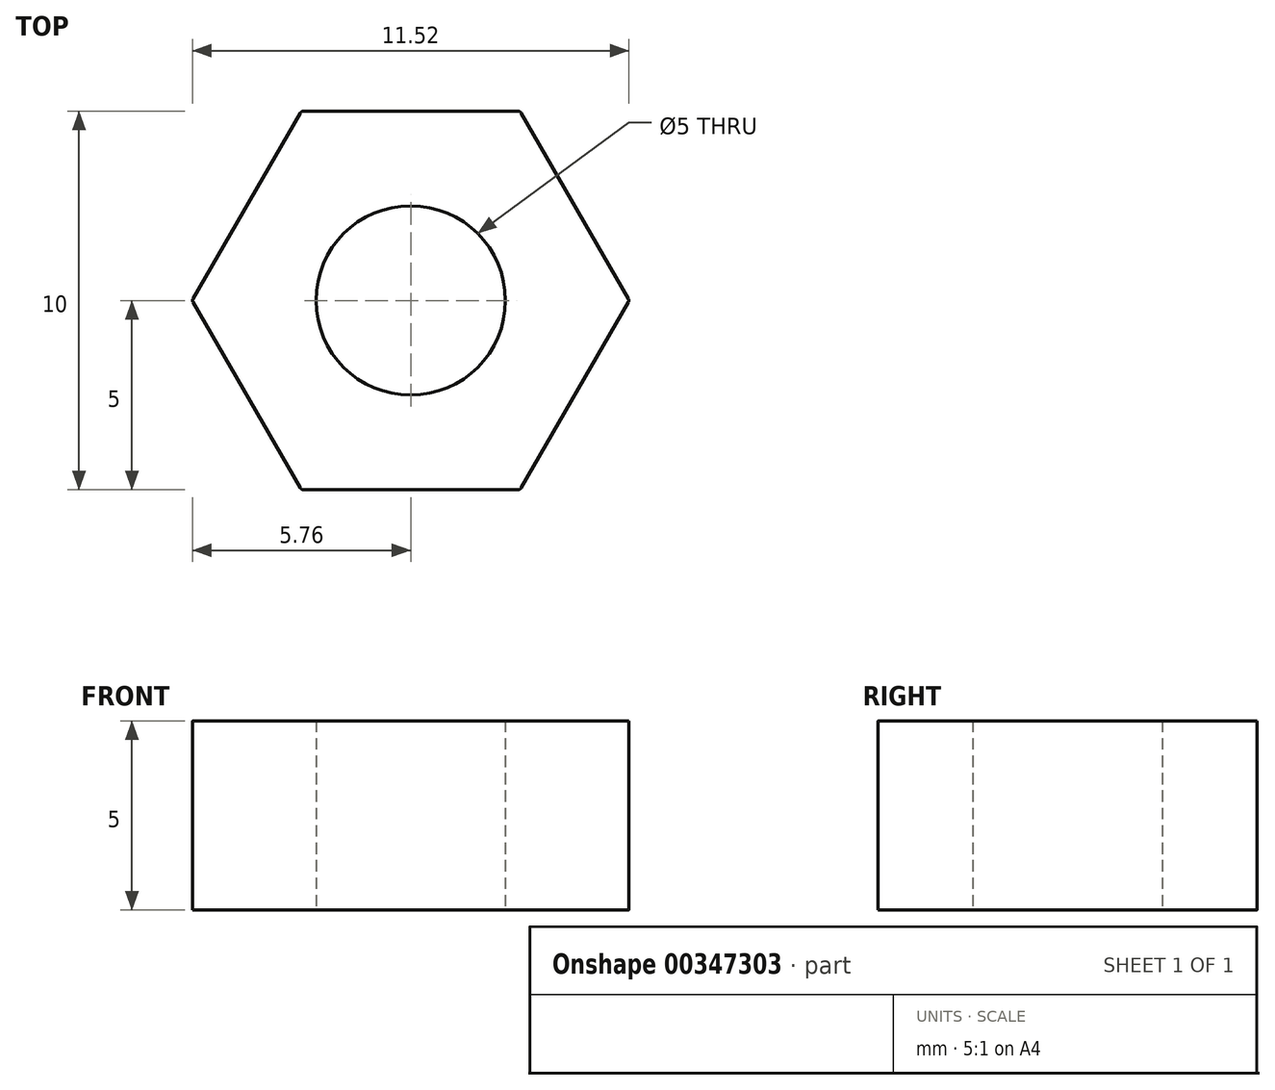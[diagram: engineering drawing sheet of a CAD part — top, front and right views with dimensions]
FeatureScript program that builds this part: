
annotation { "Feature Type Name" : "Feature", "Feature Type Description" : "" }
export const myFeature = defineFeature(function(context is Context, id is Id, definition is map)
    precondition{}
    {
        {
            var Q0;
            Q0=qCreatedBy(makeId("Top.planeOp"),FACE);
            var sketch = newSketch(context, id + "F0", { "sketchPlane" : qUnion([Q0])});
            skCircle(sketch, "E0.cCircle", {"center": v(0, 0) * mm, "radius": 5 * mm, "construction": true});
            skLineSegment(sketch, "E0.0", {"start": v(5.77, 0) * mm, "end": v(2.89, -5) * mm});
            skLineSegment(sketch, "E0.1", {"start": v(2.89, -5) * mm, "end": v(-2.89, -5) * mm});
            skLineSegment(sketch, "E0.2", {"start": v(-2.89, -5) * mm, "end": v(-5.77, 0) * mm});
            skLineSegment(sketch, "E0.3", {"start": v(-5.77, 0) * mm, "end": v(-2.89, 5) * mm});
            skLineSegment(sketch, "E0.4", {"start": v(-2.89, 5) * mm, "end": v(2.89, 5) * mm});
            skLineSegment(sketch, "E0.5", {"start": v(2.89, 5) * mm, "end": v(5.77, 0) * mm});
            skPoint(sketch, "E0.0.midPoint", {"position": v(4.33, -2.5) * mm});
            skCircle(sketch, "E1", {"center": v(0, 0) * mm, "radius": 2.5 * mm});
            skSolve(sketch);
        }
        {
            var Q0;
            Q0 = qSketchRegion(id + "F0", true);
            extrude(context, id + "F1", {"entities" : qUnion([Q0]), "depth" : 5 * mm});
        }
        {
            var Q0;
            Q0=makeQuery(id+"F1.opExtrude","SWEPT_EDGE",EDGE,{"disambiguationData":[OSD([sQuery(id+"F0.wireOp",EDGE,"E0.0"),sQuery(id+"F0.wireOp",EDGE,"E0.5")])]});
            var Q1;
            Q1=makeQuery(id+"F1.opExtrude","SWEPT_EDGE",EDGE,{"disambiguationData":[OSD([sQuery(id+"F0.wireOp",EDGE,"E0.4"),sQuery(id+"F0.wireOp",EDGE,"E0.5")])]});
            var Q2;
            Q2=makeQuery(id+"F1.opExtrude","SWEPT_EDGE",EDGE,{"disambiguationData":[OSD([sQuery(id+"F0.wireOp",EDGE,"E0.3"),sQuery(id+"F0.wireOp",EDGE,"E0.4")])]});
            var Q3;
            Q3=makeQuery(id+"F1.opExtrude","SWEPT_EDGE",EDGE,{"disambiguationData":[OSD([sQuery(id+"F0.wireOp",EDGE,"E0.0"),sQuery(id+"F0.wireOp",EDGE,"E0.1")])]});
            var Q4;
            Q4=makeQuery(id+"F1.opExtrude","SWEPT_EDGE",EDGE,{"disambiguationData":[OSD([sQuery(id+"F0.wireOp",EDGE,"E0.2"),sQuery(id+"F0.wireOp",EDGE,"E0.3")])]});
            var Q5;
            Q5=makeQuery(id+"F1.opExtrude","SWEPT_EDGE",EDGE,{"disambiguationData":[OSD([sQuery(id+"F0.wireOp",EDGE,"E0.1"),sQuery(id+"F0.wireOp",EDGE,"E0.2")])]});
            fillet(context, id + "F2", {"entities" : qUnion([Q0, Q1, Q2, Q3, Q4, Q5]), "radius" : 0.1 * mm, "tangentPropagation" : true, "allowEdgeOverflow" : false});
        }
    });
